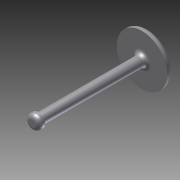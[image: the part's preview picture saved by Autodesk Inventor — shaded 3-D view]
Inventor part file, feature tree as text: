
AUTODESK INVENTOR PART (.ipt)
format: ipt  version: 2012 (Build 160160000, 160)  size: 115,712 bytes
history: native  units: in
note: dims shown in document units (in); Inventor stores cm internally (conversion verified against a paired STEP export)
features: extrude x3, sketch x3, fillet x2, reference x1
ambient origin geometry x8: Origin, YZ Plane, XZ Plane, XY Plane, X Axis, Y Axis, Z Axis, Center Point
bodies: Solid1 (feature_tree)
feature tree (9):
  extrude  "Extrusion1"  Depth=1.5748in
  extrude  "Extrusion2"  Depth=0.4454in
  fillet  "Fillet2"  Radius=0.1875in
  extrude  "Extrusion3"  Depth=0.0625in
  fillet  "Fillet3"  Radius=0.125in
  sketch  "Sketch1"  dims[d0=3.0625in d1=0.188in d2=0.0in d3=0.0in d5=1.5748in]
  reference  "Reference1"
  sketch  "Sketch2"  dims[d6=0.1875in d7=0.0in d9=0.4454in d10=0.1875in d11=0.0in]
  sketch  "Sketch3"  dims[d12=0.0625in d13=0.0625in d14=0.125in d15=0.0946in d16=0.125in]
